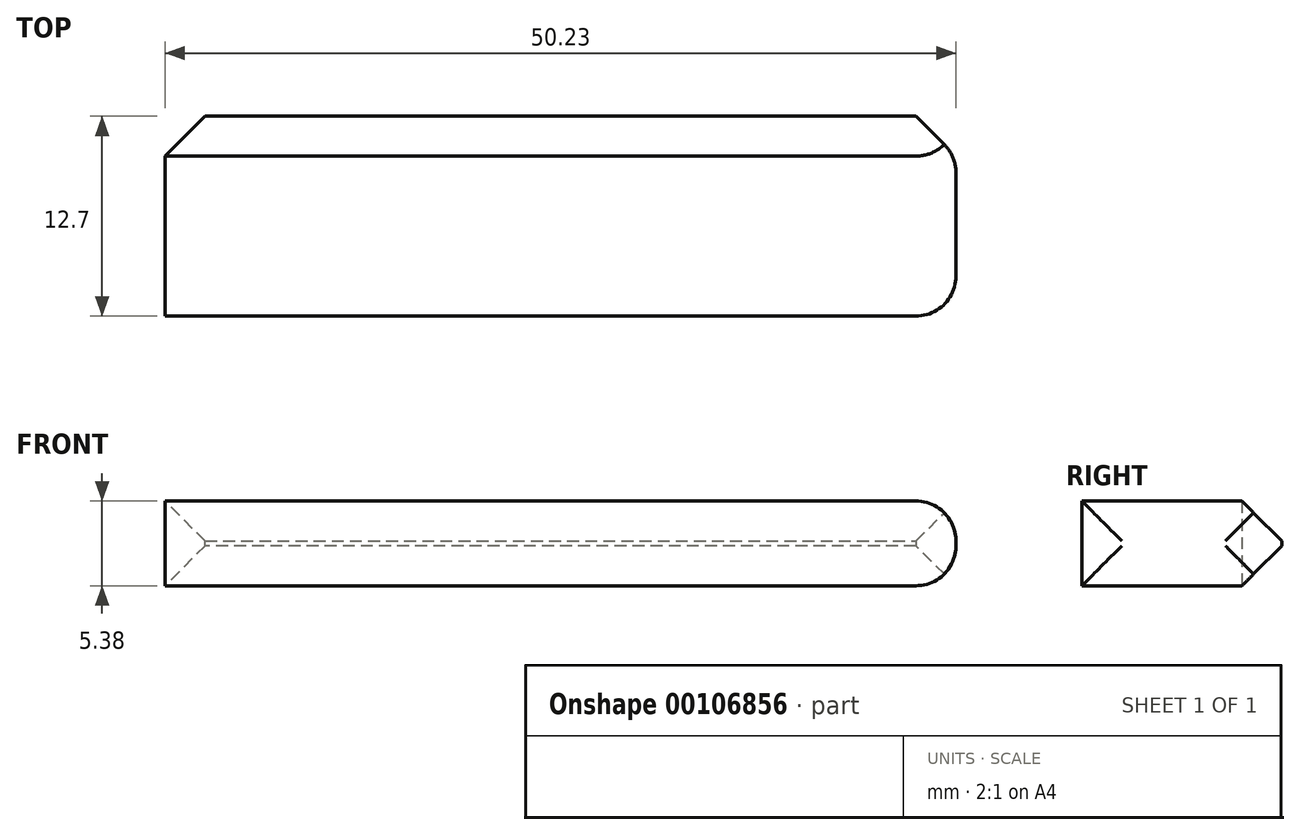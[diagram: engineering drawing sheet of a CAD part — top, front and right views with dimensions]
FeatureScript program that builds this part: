
annotation { "Feature Type Name" : "Feature", "Feature Type Description" : "" }
export const myFeature = defineFeature(function(context is Context, id is Id, definition is map)
    precondition{}
    {
        {
            var Q0;
            Q0=qCreatedBy(makeId("Front.planeOp"),FACE);
            var sketch = newSketch(context, id + "F0", { "sketchPlane" : qUnion([Q0])});
            skCircle(sketch, "E0", {"center": v(0, 0) * mm, "radius": 4.04 * mm});
            skLineSegment(sketch, "E1.bottom", {"start": v(3.23, 2.42) * mm, "end": v(53.77, 2.42) * mm});
            skLineSegment(sketch, "E1.top", {"start": v(3.23, -2.67) * mm, "end": v(53.77, -2.67) * mm});
            skLineSegment(sketch, "E1.left", {"start": v(3.23, 2.42) * mm, "end": v(3.23, -2.67) * mm});
            skLineSegment(sketch, "E1.right", {"start": v(53.77, 2.42) * mm, "end": v(53.77, -2.67) * mm});
            skSolve(sketch);
        }
        {
            var Q0;
            {var subQ4=sQuery(id+"F0.wireOp",EDGE,"E1.bottom");Q0=makeQuery(id+"F0.imprint","IMPRINT",FACE,{"disambiguationData":[TD([[makeQuery(id+"F0.imprint","IMPRINT",EDGE,{"derivedFrom":subQ4}),-1.0]])]});}
            extrude(context, id + "F1", {"entities" : qUnion([Q0]), "depth" : 1.27 * mm});
        }
        {
            var Q0;
            Q0=makeQuery(id+"F1.opExtrude","CAP_FACE",FACE,{"disambiguationData":[OSD([sQuery(id+"F0.wireOp",EDGE,"E0"),sQuery(id+"F0.wireOp",EDGE,"E1.bottom"),sQuery(id+"F0.wireOp",EDGE,"E1.top"),sQuery(id+"F0.wireOp",EDGE,"E1.left"),sQuery(id+"F0.wireOp",EDGE,"E1.right")])],"isStart":false});
            var sketch = newSketch(context, id + "F2", { "sketchPlane" : qUnion([Q0])});
            skLineSegment(sketch, "E2.bottom", {"start": v(0, 0) * mm, "end": v(-50.23, 0) * mm});
            skLineSegment(sketch, "E2.top", {"start": v(0, 5.38) * mm, "end": v(-50.23, 5.38) * mm});
            skLineSegment(sketch, "E2.left", {"start": v(0, 0) * mm, "end": v(0, 5.38) * mm});
            skLineSegment(sketch, "E2.right", {"start": v(-50.23, 0) * mm, "end": v(-50.23, 5.38) * mm});
            skSolve(sketch);
        }
        {
            var Q0;
            Q0 = qSketchRegion(id + "F2", true);
            extrude(context, id + "F3", {"entities" : qUnion([Q0]), "depth" : 12.7 * mm});
        }
        {
            var Q0;
            Q0=makeQuery(id+"F1.opExtrude","SWEPT_BODY",BODY,{"disambiguationData":[OSD([sQuery(id+"F0.wireOp",EDGE,"E0"),sQuery(id+"F0.wireOp",EDGE,"E1.bottom"),sQuery(id+"F0.wireOp",EDGE,"E1.top"),sQuery(id+"F0.wireOp",EDGE,"E1.left"),sQuery(id+"F0.wireOp",EDGE,"E1.right")])]});
            deleteBodies(context, id + "F4", {"entities" : qUnion([Q0])});
        }
        {
            var Q0;
            Q0=makeQuery(id+"F3.opExtrude","CAP_FACE",FACE,{"disambiguationData":[OSD([sQuery(id+"F2.wireOp",EDGE,"E2.bottom"),sQuery(id+"F2.wireOp",EDGE,"E2.top"),sQuery(id+"F2.wireOp",EDGE,"E2.left"),sQuery(id+"F2.wireOp",EDGE,"E2.right")])],"isStart":true});
            chamfer(context, id + "F5", {"entities" : qUnion([Q0]), "width" : 2.54 * mm, "tangentPropagation" : true});
        }
        {
            var Q0;
            Q0=makeQuery(id+"F3.opExtrude","SWEPT_FACE",FACE,{"disambiguationData":[OSD([sQuery(id+"F2.wireOp",EDGE,"E2.left")])]});
            fillet(context, id + "F6", {"entities" : qUnion([Q0]), "radius" : 2.54 * mm, "tangentPropagation" : true, "allowEdgeOverflow" : false});
        }
    });
